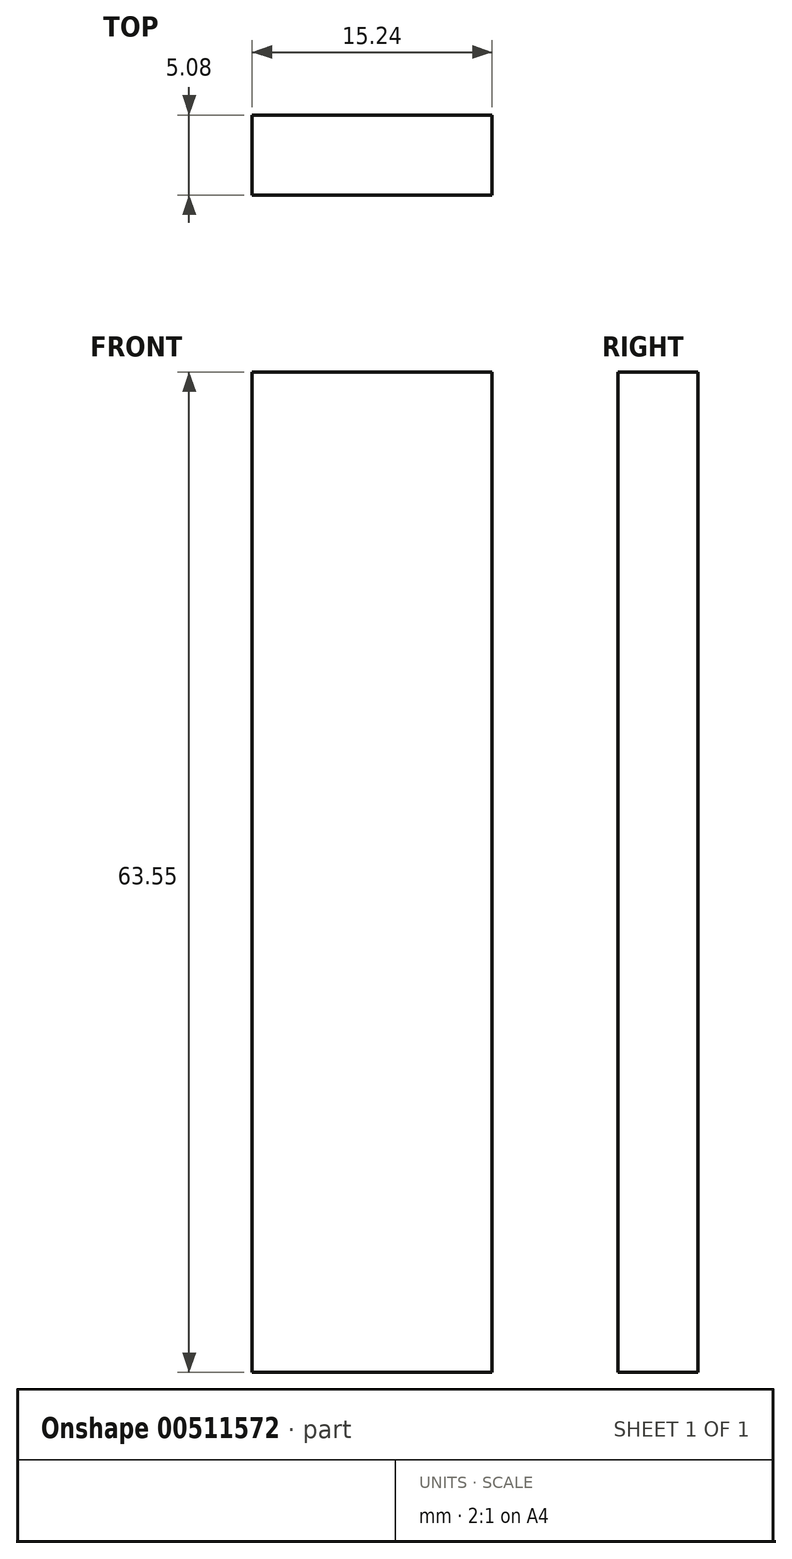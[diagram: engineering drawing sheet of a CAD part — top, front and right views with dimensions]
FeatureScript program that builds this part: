
annotation { "Feature Type Name" : "Feature", "Feature Type Description" : "" }
export const myFeature = defineFeature(function(context is Context, id is Id, definition is map)
    precondition{}
    {
        {
            var Q0;
            Q0=qCreatedBy(makeId("Front.planeOp"),FACE);
            var sketch = newSketch(context, id + "F0", { "sketchPlane" : qUnion([Q0])});
            skLineSegment(sketch, "E0", {"start": v(0, 0) * mm, "end": v(15.24, 0) * mm});
            skLineSegment(sketch, "E1", {"start": v(15.24, 0) * mm, "end": v(15.24, 63.55) * mm});
            skLineSegment(sketch, "E2", {"start": v(15.24, 63.55) * mm, "end": v(0, 63.55) * mm});
            skLineSegment(sketch, "E3", {"start": v(0, 63.55) * mm, "end": v(0, 0) * mm});
            skSolve(sketch);
        }
        {
            var Q0;
            Q0 = qSketchRegion(id + "F0", true);
            extrude(context, id + "F1", {"entities" : qUnion([Q0]), "depth" : 5.08 * mm, "offsetDistance" : 25.4 * mm});
        }
    });
